# Revit family: oventrop_hydrocontrol-vfr_1062350rfa
name_source: partatom
category: Арматура трубопроводов
revit_build: Autodesk Revit 2017 (Build: 20160225_1515(x64)
units: mm (PartAtom-declared; Revit-internal decimal feet)

## family parameters
Всегда вертикально = Да
Заголовок OmniClass = Adjusting/Controlling Valves for Liquid Services
На основе рабочей плоскости = Нет
Номер OmniClass = 23.65.55.14.17
Общий = Нет
При загрузке вырезать с полостями = Нет
Размер круглого соединителя = Использовать радиус
Тип детали = Клапан - Вставляется

## types (1)
- DN 50
    Angle = 60.00°
    Angle 2 = 30.00°
    Angle 3 = -60.00°
    Article Description = Balancing valve with flanges according to DIN, PN 16
    Article Type = Hydrocontrol VFR 10623 DN 50
    Black = Color RGB 35-35-35
    Bronze = Color RGB 156-122-90
    CurDst = 19 мм
    Custom = Нет
    Dst1 = 23 мм
    DstChk = 23 мм
    EMCS Version = 2.0
    ETIM Article Class = EC011463
    Family Version = 10.14
    FlangeDiameter = 165 мм
    GTIN = 4026755253832
    H = 148 мм
    Hb1 = 150 мм
    Hb2 = 42 мм
    Hb3 = 10 мм
    Hb4 = 18 мм
    Hb5 = 3 мм
    Hb6 = 42 мм
    Height = 145 мм
    Hlp1 = 22 мм
    Hlp2 = 6 мм
    IFCExportAs = IfcValveType
    IFCExportType = PRESSUREREDUCING
    L2 = 19 мм
    Length = 230 мм
    Lgt1 = 2 мм
    Lgt2 = 15 мм
    Lgt3 = 32 мм
    Lgt4 = 110 мм
    MEPcontent Class = VALVE_BALANCING
    Manufacturer Art. No. = 1062350
    Manufacturer URL = http://www.oventrop.de
    NominalDiameter = 50 мм
    NominalRadius = 25 мм
    OuterDiameter = 60 мм
    Pressure Drop = 0.0 Па
    Product Line = Oventrop
    R1 = 9 мм
    R2 = 10 мм
    Rad1 = 63 мм
    Rad2 = 83 мм
    Rad3 = 35 мм
    Rad4 = 32 мм
    Rad5 = 35 мм
    Rad6 = 25 мм
    Rad7 = 37 мм
    RegulatorRadius = 35 мм
    Revit Version = 2015
    URL = http://file-system.ru
    VDst = 27 мм
    VHth = 42 мм
    r1 = 2 мм
    r2 = 3 мм
    Группа модели = Hydrocontrol VFR 10623 DN 50
    Изготовитель = Oventrop
    Описание = Balancing valve with flanges according to DIN, PN 16

## geometry (parser evidence)
native form markers: Blend x2, Sweep x3
no freeform markers — native parametric forms only
